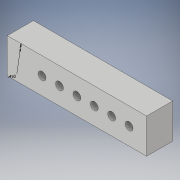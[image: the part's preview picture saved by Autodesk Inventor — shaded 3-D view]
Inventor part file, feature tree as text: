
AUTODESK INVENTOR PART (.ipt)
format: ipt  version: 2018 (Build 220112000, 112)  size: 126,464 bytes
history: native  units: in
note: dims shown in document units (in); Inventor stores cm internally (conversion verified against a paired STEP export)
features: extrude x4, sketch x3, pattern_linear x1, projected_geometry x1
ambient origin geometry x8: Origin, YZ Plane, XZ Plane, XY Plane, X Axis, Y Axis, Z Axis, Center Point
bodies: Solid1 (feature_tree)
feature tree (9):
  sketch  "Sketch1"  dims[d0=0.45in d1=2.0in]
  extrude  "Extrusion1"  Depth=2.0in
  extrude  "Extrusion2"  Depth=1.5in TaperAngle=0.0deg
  pattern_linear  "Rectangular Pattern1"  Count1=6 Spacing1=1.0in
  sketch  "Sketch2"  dims[d2=8.0in d3=1.5in d4=0.0in]
  extrude  "Extrusion3"  Depth=1.0in
  extrude  "Extrusion4"  Depth=1.0in TaperAngle=0.0deg
  sketch  "Sketch3"  dims[d5=1.5in d6=0.0in d7=2.3622in d9=1.0in d10=0.45in d11=7.25in d12=0.0in d13=1.0in d14=0.0in]
  projected_geometry  "Projected Loop1"
